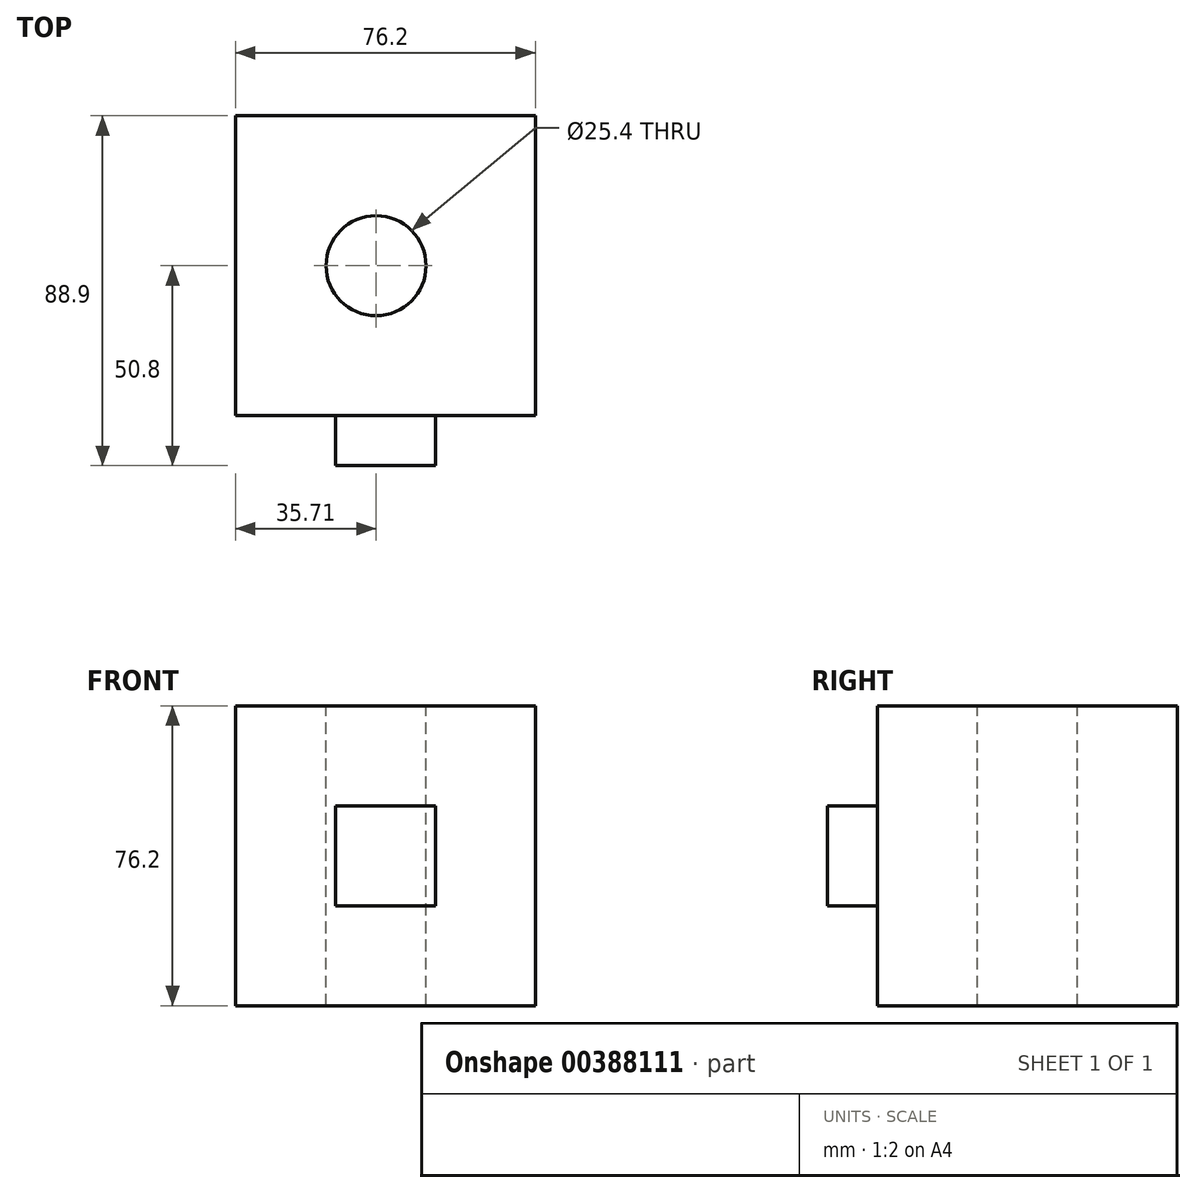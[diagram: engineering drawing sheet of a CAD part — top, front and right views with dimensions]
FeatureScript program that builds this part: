
annotation { "Feature Type Name" : "Feature", "Feature Type Description" : "" }
export const myFeature = defineFeature(function(context is Context, id is Id, definition is map)
    precondition{}
    {
        {
            var Q0;
            Q0=qCreatedBy(makeId("Front.planeOp"),FACE);
            var sketch = newSketch(context, id + "F0", { "sketchPlane" : qUnion([Q0])});
            skLineSegment(sketch, "E0.bottom", {"start": v(-35.7, 28.28) * mm, "end": v(40.5, 28.28) * mm});
            skLineSegment(sketch, "E0.top", {"start": v(-35.7, -47.92) * mm, "end": v(40.5, -47.92) * mm});
            skLineSegment(sketch, "E0.left", {"start": v(-35.7, 28.28) * mm, "end": v(-35.7, -47.92) * mm});
            skLineSegment(sketch, "E0.right", {"start": v(40.5, 28.28) * mm, "end": v(40.5, -47.92) * mm});
            skSolve(sketch);
        }
        {
            var Q0;
            Q0 = qSketchRegion(id + "F0", true);
            extrude(context, id + "F1", {"entities" : qUnion([Q0]), "depth" : 76.2 * mm});
        }
        {
            var Q0;
            Q0=makeQuery(id+"F1.opExtrude","SWEPT_FACE",FACE,{"disambiguationData":[OSD([sQuery(id+"F0.wireOp",EDGE,"E0.bottom")])]});
            var sketch = newSketch(context, id + "F2", { "sketchPlane" : qUnion([Q0])});
            skPoint(sketch, "E1", {"position": v(0, -38.1) * mm});
            skPoint(sketch, "E1.positionSnap0", {"position": v(-35.7, -38.1) * mm});
            skSolve(sketch);
        }
        {
            var Q0;
            Q0=sQuery(id+"F2.wireOp",VERTEX,"E1");
            var Q1;
            Q1=makeQuery(id+"F1.opExtrude","SWEPT_BODY",BODY,{"disambiguationData":[OSD([sQuery(id+"F0.wireOp",EDGE,"E0.bottom"),sQuery(id+"F0.wireOp",EDGE,"E0.top"),sQuery(id+"F0.wireOp",EDGE,"E0.left"),sQuery(id+"F0.wireOp",EDGE,"E0.right")])]});
            hole(context, id + "F3", {"style" : HoleStyle.SIMPLE, "endStyle" : HoleEndStyle.THROUGH, "holeDiameter" : 25.4 * mm, "isTappedThrough" : true, "tappedDepth" : 12.7 * mm, "tapClearance" : 3, "locations" : qUnion([Q0]), "scope" : qUnion([Q1])});
        }
        {
            var Q0;
            Q0=makeQuery(id+"F1.opExtrude","CAP_FACE",FACE,{"disambiguationData":[OSD([sQuery(id+"F0.wireOp",EDGE,"E0.bottom"),sQuery(id+"F0.wireOp",EDGE,"E0.top"),sQuery(id+"F0.wireOp",EDGE,"E0.left"),sQuery(id+"F0.wireOp",EDGE,"E0.right")])],"isStart":false});
            var sketch = newSketch(context, id + "F4", { "sketchPlane" : qUnion([Q0])});
            skLineSegment(sketch, "E2.bottom", {"start": v(-10.3, 2.88) * mm, "end": v(15.1, 2.88) * mm});
            skLineSegment(sketch, "E2.top", {"start": v(-10.3, -22.52) * mm, "end": v(15.1, -22.52) * mm});
            skLineSegment(sketch, "E2.left", {"start": v(-10.3, 2.88) * mm, "end": v(-10.3, -22.52) * mm});
            skLineSegment(sketch, "E2.right", {"start": v(15.1, 2.88) * mm, "end": v(15.1, -22.52) * mm});
            skSolve(sketch);
        }
        {
            var Q0;
            Q0=makeQuery(id+"F4.imprint","IMPRINT",FACE,{"disambiguationData":[TD([[makeQuery(id+"F4.imprint","IMPRINT",EDGE,{"derivedFrom":sQuery(id+"F4.wireOp",EDGE,"E2.bottom")}),-1.0]])]});
            extrude(context, id + "F5", {"entities" : qUnion([Q0]), "operationType" : NewBodyOperationType.ADD, "depth" : 12.7 * mm});
        }
    });
